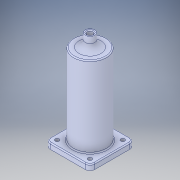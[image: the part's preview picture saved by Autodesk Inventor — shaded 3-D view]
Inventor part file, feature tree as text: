
AUTODESK INVENTOR PART (.ipt)
format: ipt  version: 2018 (Build 220112000, 112)  size: 256,512 bytes
history: native  units: in
note: dims shown in document units (in); Inventor stores cm internally (conversion verified against a paired STEP export)
features: extrude x8, sketch x7, projected_geometry x5, fillet x3, revolve x1, chamfer x1, other x1
ambient origin geometry x8: Origin, YZ Plane, XZ Plane, XY Plane, X Axis, Y Axis, Z Axis, Center Point
bodies: Solid1 (feature_tree)
feature tree (26):
  extrude  "Extrusion1"  TaperAngle=0.0deg  [1 undecoded]
  sketch  "Sketch2"  dims[d4=0.3937in d5=0.0in d6=1.0in d7=0.0in]
  extrude  "Extrusion2"  Depth=1.0in TaperAngle=0.0deg
  extrude  "Extrusion3"  Depth=0.9252in
  sketch  "Sketch3"  dims[d8=2.0in d9=0.0in d10=0.9252in]
  extrude  "Extrusion4"  Depth=2.0in TaperAngle=0.0deg
  extrude  "Extrusion5"  Depth=1.0in
  extrude  "Extrusion6"  Depth=1.0in TaperAngle=0.0deg
  fillet  "Fillet2"  Radius=0.125in
  fillet  "Fillet3"  Radius=1.374in
  extrude  "Extrusion7"  Depth=0.0625in TaperAngle=45.0deg
  extrude  "Extrusion8"  [1 undecoded]
  revolve  "Revolution1"  [1 undecoded]
  chamfer  "Chamfer1"  [1 undecoded]
  fillet  "Fillet1"  [1 undecoded]
  sketch  "Sketch1"  dims[d0=0.0in d1=0.0in d2=0.0in d3=0.0in]
  projected_geometry  "Projected Loop1"
  projected_geometry  "Projected Loop2"
  projected_geometry  "Projected Loop3"
  sketch  "Sketch4"  dims[d11=0.45in d12=2.0in d13=0.0in]
  sketch  "Sketch5"  dims[d14=0.5in d15=1.0in]
  projected_geometry  "Projected Loop4"
  sketch  "Sketch6"  dims[d16=0.25in d17=0.0in d18=1.0in d19=0.0in d20=0.125in d21=1.374in]
  projected_geometry  "Projected Loop5"
  sketch  "Sketch7"  dims[d22=90.0deg d23=0.0625in d24=0.0787in d25=45.0deg]
  other  "Ø8.0mm Dowel Hole1"
note: 5 required parameter values undecoded (feature->parameter linkage not recoverable at this tier; creation-order binding heuristic only, values carry confidence <= 0.55)
